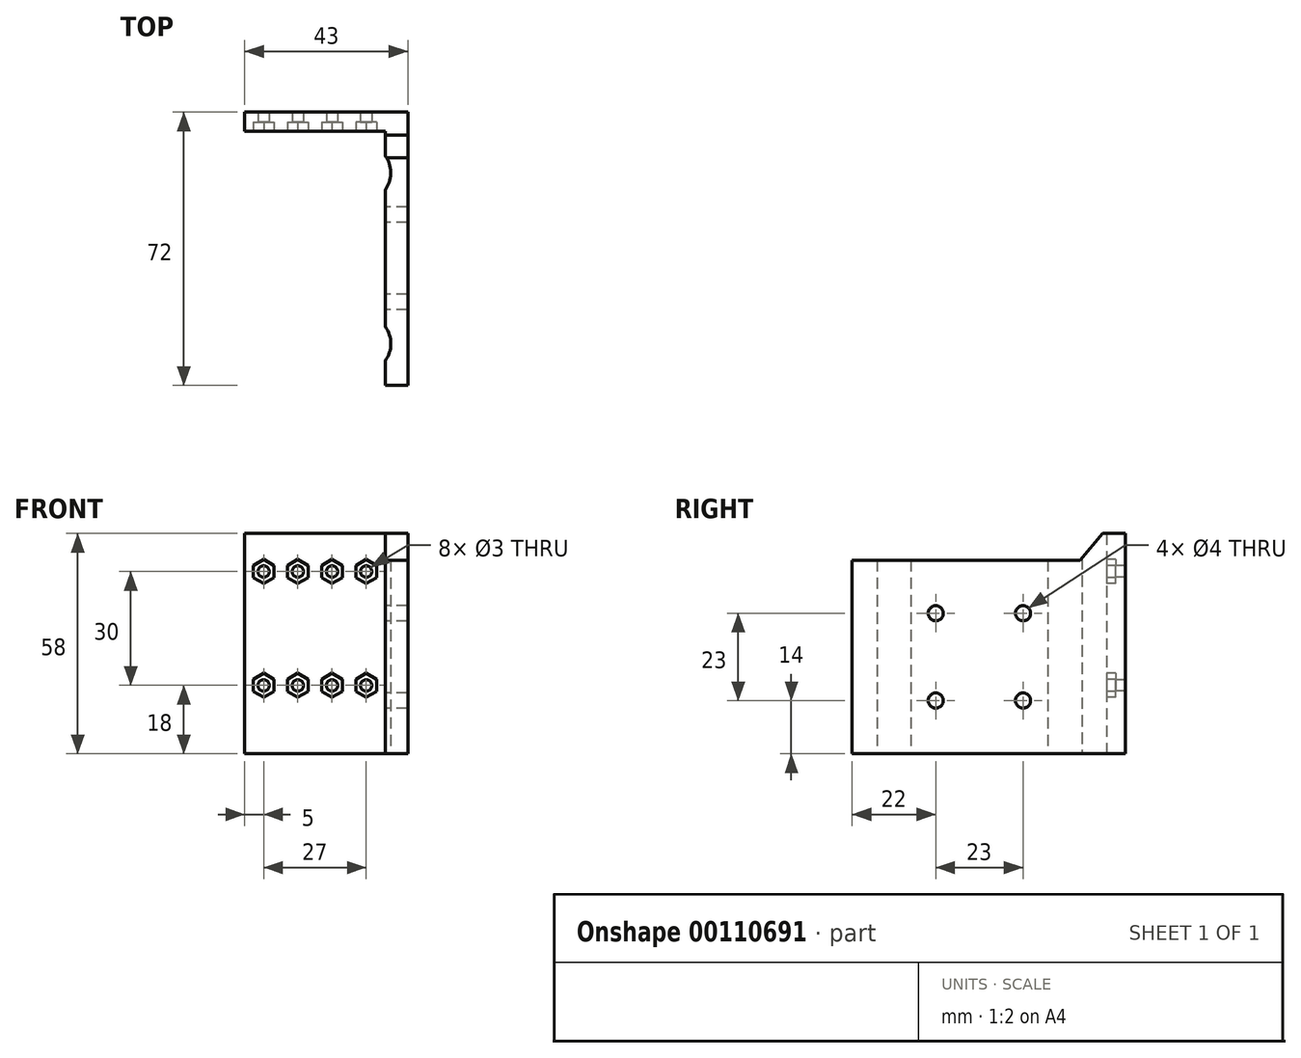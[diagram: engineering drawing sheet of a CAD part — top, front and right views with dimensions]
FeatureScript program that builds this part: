
annotation { "Feature Type Name" : "Feature", "Feature Type Description" : "" }
export const myFeature = defineFeature(function(context is Context, id is Id, definition is map)
    precondition{}
    {
        {
            var Q0;
            Q0=qCreatedBy(makeId("Top.planeOp"),FACE);
            var sketch = newSketch(context, id + "F0", { "sketchPlane" : qUnion([Q0])});
            skLineSegment(sketch, "E0", {"start": v(0, 0) * mm, "end": v(0, 67) * mm});
            skLineSegment(sketch, "E1", {"start": v(0, 67) * mm, "end": v(-37, 67) * mm});
            skLineSegment(sketch, "E2", {"start": v(-37, 67) * mm, "end": v(-37, 72) * mm});
            skLineSegment(sketch, "E3", {"start": v(-37, 72) * mm, "end": v(6, 72) * mm});
            skLineSegment(sketch, "E4", {"start": v(6, 72) * mm, "end": v(6, 0) * mm});
            skLineSegment(sketch, "E5", {"start": v(6, 0) * mm, "end": v(0, 0) * mm});
            skSolve(sketch);
        }
        {
            var Q0;
            Q0 = qSketchRegion(id + "F0", true);
            extrude(context, id + "F1", {"entities" : qUnion([Q0]), "depth" : 58 * mm});
        }
        {
            var Q0;
            Q0=makeQuery(id+"F1.opExtrude","SWEPT_FACE",FACE,{"disambiguationData":[OSD([sQuery(id+"F0.wireOp",EDGE,"E0")])]});
            var sketch = newSketch(context, id + "F2", { "sketchPlane" : qUnion([Q0])});
            skLineSegment(sketch, "E6", {"start": v(-33.5, 0) * mm, "end": v(-33.5, 58) * mm, "construction": true});
            skCircle(sketch, "E7", {"center": v(-45, 14) * mm, "radius": 2 * mm});
            skCircle(sketch, "E8", {"center": v(-45, 37) * mm, "radius": 2 * mm});
            skCircle(sketch, "E9", {"center": v(-22, 14) * mm, "radius": 2 * mm});
            skCircle(sketch, "E10", {"center": v(-22, 37) * mm, "radius": 2 * mm});
            skLineSegment(sketch, "E11", {"start": v(0, 25.5) * mm, "end": v(-67, 25.5) * mm, "construction": true});
            skSolve(sketch);
        }
        {
            var Q0;
            Q0=makeQuery(id+"F2.imprint","IMPRINT",FACE,{"disambiguationData":[TD([[makeQuery(id+"F2.imprint","IMPRINT",EDGE,{"derivedFrom":sQuery(id+"F2.wireOp",EDGE,"E8")}),1.0]])]});
            var Q1;
            Q1=makeQuery(id+"F2.imprint","IMPRINT",FACE,{"disambiguationData":[TD([[makeQuery(id+"F2.imprint","IMPRINT",EDGE,{"derivedFrom":sQuery(id+"F2.wireOp",EDGE,"E7")}),1.0]])]});
            var Q2;
            Q2=makeQuery(id+"F2.imprint","IMPRINT",FACE,{"disambiguationData":[TD([[makeQuery(id+"F2.imprint","IMPRINT",EDGE,{"derivedFrom":sQuery(id+"F2.wireOp",EDGE,"E9")}),1.0]])]});
            var Q3;
            Q3=makeQuery(id+"F2.imprint","IMPRINT",FACE,{"disambiguationData":[TD([[makeQuery(id+"F2.imprint","IMPRINT",EDGE,{"derivedFrom":sQuery(id+"F2.wireOp",EDGE,"E10")}),1.0]])]});
            extrude(context, id + "F3", {"entities" : qUnion([Q0, Q1, Q2, Q3]), "operationType" : NewBodyOperationType.REMOVE, "endBound" : BoundingType.THROUGH_ALL, "oppositeDirection" : true, "depth" : 25 * mm});
        }
        {
            var Q0;
            Q0=makeQuery(id+"F0.imprint","IMPRINT",FACE,{"disambiguationData":[TD([[makeQuery(id+"F0.imprint","IMPRINT",EDGE,{"derivedFrom":sQuery(id+"F0.wireOp",EDGE,"E0")}),-1.0]])]});
            var sketch = newSketch(context, id + "F4", { "sketchPlane" : qUnion([Q0])});
            skLineSegment(sketch, "E12", {"start": v(0, 33.5) * mm, "end": v(25.28, 33.5) * mm, "construction": true});
            skCircle(sketch, "E13", {"center": v(-6, 11) * mm, "radius": 7.5 * mm});
            skCircle(sketch, "E14.MirrorC", {"center": v(-6, 56) * mm, "radius": 7.5 * mm});
            skSolve(sketch);
        }
        {
            var Q0;
            Q0 = qSketchRegion(id + "F4", true);
            extrude(context, id + "F5", {"entities" : qUnion([Q0]), "operationType" : NewBodyOperationType.REMOVE, "endBound" : BoundingType.THROUGH_ALL, "depth" : 25 * mm});
        }
        {
            var Q0;
            Q0=makeQuery(id+"F1.opExtrude","SWEPT_FACE",FACE,{"disambiguationData":[OSD([sQuery(id+"F0.wireOp",EDGE,"E4")])]});
            var sketch = newSketch(context, id + "F6", { "sketchPlane" : qUnion([Q0])});
            skLineSegment(sketch, "E15", {"start": v(66, 58) * mm, "end": v(60, 51) * mm});
            skLineSegment(sketch, "E16", {"start": v(60, 51) * mm, "end": v(0, 51) * mm});
            skLineSegment(sketch, "E17", {"start": v(0, 51) * mm, "end": v(0, 58) * mm});
            skLineSegment(sketch, "E18", {"start": v(0, 58) * mm, "end": v(66, 58) * mm});
            skSolve(sketch);
        }
        {
            var Q0;
            Q0 = qSketchRegion(id + "F6", true);
            extrude(context, id + "F7", {"entities" : qUnion([Q0]), "operationType" : NewBodyOperationType.REMOVE, "endBound" : BoundingType.THROUGH_ALL, "oppositeDirection" : true, "depth" : 25 * mm});
        }
        {
            var Q0;
            Q0=makeQuery(id+"F1.opExtrude","SWEPT_FACE",FACE,{"disambiguationData":[OSD([sQuery(id+"F0.wireOp",EDGE,"E1")])]});
            var sketch = newSketch(context, id + "F8", { "sketchPlane" : qUnion([Q0])});
            skLineSegment(sketch, "E19", {"start": v(0, 33) * mm, "end": v(-37, 33) * mm, "construction": true});
            skCircle(sketch, "E20", {"center": v(-5, 48) * mm, "radius": 1.5 * mm});
            skCircle(sketch, "E21.cCircle", {"center": v(-5, 48) * mm, "radius": 2.75 * mm, "construction": true});
            skLineSegment(sketch, "E21.0", {"start": v(-7.75, 46.41) * mm, "end": v(-7.75, 49.59) * mm});
            skLineSegment(sketch, "E21.1", {"start": v(-7.75, 49.59) * mm, "end": v(-5, 51.18) * mm});
            skLineSegment(sketch, "E21.2", {"start": v(-5, 51.18) * mm, "end": v(-2.25, 49.59) * mm});
            skLineSegment(sketch, "E21.3", {"start": v(-2.25, 49.59) * mm, "end": v(-2.25, 46.41) * mm});
            skLineSegment(sketch, "E21.4", {"start": v(-2.25, 46.41) * mm, "end": v(-5, 44.82) * mm});
            skLineSegment(sketch, "E21.5", {"start": v(-5, 44.82) * mm, "end": v(-7.75, 46.41) * mm});
            skPoint(sketch, "E21.0.midPoint", {"position": v(-7.75, 48) * mm});
            skCircle(sketch, "E22.0.1.0", {"center": v(-5, 18) * mm, "radius": 1.5 * mm});
            skCircle(sketch, "E22.0.1.1", {"center": v(-5, 18) * mm, "radius": 2.75 * mm, "construction": true});
            skPoint(sketch, "E22.0.1.2", {"position": v(-7.75, 18) * mm});
            skLineSegment(sketch, "E22.0.1.3", {"start": v(-2.25, 19.59) * mm, "end": v(-2.25, 16.41) * mm});
            skLineSegment(sketch, "E22.0.1.4", {"start": v(-2.25, 16.41) * mm, "end": v(-5, 14.82) * mm});
            skLineSegment(sketch, "E22.0.1.5", {"start": v(-5, 14.82) * mm, "end": v(-7.75, 16.41) * mm});
            skLineSegment(sketch, "E22.0.1.6", {"start": v(-7.75, 16.41) * mm, "end": v(-7.75, 19.59) * mm});
            skLineSegment(sketch, "E22.0.1.7", {"start": v(-7.75, 19.59) * mm, "end": v(-5, 21.18) * mm});
            skLineSegment(sketch, "E22.0.1.8", {"start": v(-5, 21.18) * mm, "end": v(-2.25, 19.59) * mm});
            skCircle(sketch, "E22.1.0.0", {"center": v(-14, 48) * mm, "radius": 1.5 * mm});
            skCircle(sketch, "E22.1.0.1", {"center": v(-14, 48) * mm, "radius": 2.75 * mm, "construction": true});
            skPoint(sketch, "E22.1.0.2", {"position": v(-16.75, 48) * mm});
            skLineSegment(sketch, "E22.1.0.3", {"start": v(-11.25, 49.59) * mm, "end": v(-11.25, 46.41) * mm});
            skLineSegment(sketch, "E22.1.0.4", {"start": v(-11.25, 46.41) * mm, "end": v(-14, 44.82) * mm});
            skLineSegment(sketch, "E22.1.0.5", {"start": v(-14, 44.82) * mm, "end": v(-16.75, 46.41) * mm});
            skLineSegment(sketch, "E22.1.0.6", {"start": v(-16.75, 46.41) * mm, "end": v(-16.75, 49.59) * mm});
            skLineSegment(sketch, "E22.1.0.7", {"start": v(-16.75, 49.59) * mm, "end": v(-14, 51.18) * mm});
            skLineSegment(sketch, "E22.1.0.8", {"start": v(-14, 51.18) * mm, "end": v(-11.25, 49.59) * mm});
            skCircle(sketch, "E22.1.1.0", {"center": v(-14, 18) * mm, "radius": 1.5 * mm});
            skCircle(sketch, "E22.1.1.1", {"center": v(-14, 18) * mm, "radius": 2.75 * mm, "construction": true});
            skPoint(sketch, "E22.1.1.2", {"position": v(-16.75, 18) * mm});
            skLineSegment(sketch, "E22.1.1.3", {"start": v(-11.25, 19.59) * mm, "end": v(-11.25, 16.41) * mm});
            skLineSegment(sketch, "E22.1.1.4", {"start": v(-11.25, 16.41) * mm, "end": v(-14, 14.82) * mm});
            skLineSegment(sketch, "E22.1.1.5", {"start": v(-14, 14.82) * mm, "end": v(-16.75, 16.41) * mm});
            skLineSegment(sketch, "E22.1.1.6", {"start": v(-16.75, 16.41) * mm, "end": v(-16.75, 19.59) * mm});
            skLineSegment(sketch, "E22.1.1.7", {"start": v(-16.75, 19.59) * mm, "end": v(-14, 21.18) * mm});
            skLineSegment(sketch, "E22.1.1.8", {"start": v(-14, 21.18) * mm, "end": v(-11.25, 19.59) * mm});
            skCircle(sketch, "E22.2.0.0", {"center": v(-23, 48) * mm, "radius": 1.5 * mm});
            skCircle(sketch, "E22.2.0.1", {"center": v(-23, 48) * mm, "radius": 2.75 * mm, "construction": true});
            skPoint(sketch, "E22.2.0.2", {"position": v(-25.75, 48) * mm});
            skLineSegment(sketch, "E22.2.0.3", {"start": v(-20.25, 49.59) * mm, "end": v(-20.25, 46.41) * mm});
            skLineSegment(sketch, "E22.2.0.4", {"start": v(-20.25, 46.41) * mm, "end": v(-23, 44.82) * mm});
            skLineSegment(sketch, "E22.2.0.5", {"start": v(-23, 44.82) * mm, "end": v(-25.75, 46.41) * mm});
            skLineSegment(sketch, "E22.2.0.6", {"start": v(-25.75, 46.41) * mm, "end": v(-25.75, 49.59) * mm});
            skLineSegment(sketch, "E22.2.0.7", {"start": v(-25.75, 49.59) * mm, "end": v(-23, 51.18) * mm});
            skLineSegment(sketch, "E22.2.0.8", {"start": v(-23, 51.18) * mm, "end": v(-20.25, 49.59) * mm});
            skCircle(sketch, "E22.2.1.0", {"center": v(-23, 18) * mm, "radius": 1.5 * mm});
            skCircle(sketch, "E22.2.1.1", {"center": v(-23, 18) * mm, "radius": 2.75 * mm, "construction": true});
            skPoint(sketch, "E22.2.1.2", {"position": v(-25.75, 18) * mm});
            skLineSegment(sketch, "E22.2.1.3", {"start": v(-20.25, 19.59) * mm, "end": v(-20.25, 16.41) * mm});
            skLineSegment(sketch, "E22.2.1.4", {"start": v(-20.25, 16.41) * mm, "end": v(-23, 14.82) * mm});
            skLineSegment(sketch, "E22.2.1.5", {"start": v(-23, 14.82) * mm, "end": v(-25.75, 16.41) * mm});
            skLineSegment(sketch, "E22.2.1.6", {"start": v(-25.75, 16.41) * mm, "end": v(-25.75, 19.59) * mm});
            skLineSegment(sketch, "E22.2.1.7", {"start": v(-25.75, 19.59) * mm, "end": v(-23, 21.18) * mm});
            skLineSegment(sketch, "E22.2.1.8", {"start": v(-23, 21.18) * mm, "end": v(-20.25, 19.59) * mm});
            skCircle(sketch, "E22.3.0.0", {"center": v(-32, 48) * mm, "radius": 1.5 * mm});
            skCircle(sketch, "E22.3.0.1", {"center": v(-32, 48) * mm, "radius": 2.75 * mm, "construction": true});
            skPoint(sketch, "E22.3.0.2", {"position": v(-34.75, 48) * mm});
            skLineSegment(sketch, "E22.3.0.3", {"start": v(-29.25, 49.59) * mm, "end": v(-29.25, 46.41) * mm});
            skLineSegment(sketch, "E22.3.0.4", {"start": v(-29.25, 46.41) * mm, "end": v(-32, 44.82) * mm});
            skLineSegment(sketch, "E22.3.0.5", {"start": v(-32, 44.82) * mm, "end": v(-34.75, 46.41) * mm});
            skLineSegment(sketch, "E22.3.0.6", {"start": v(-34.75, 46.41) * mm, "end": v(-34.75, 49.59) * mm});
            skLineSegment(sketch, "E22.3.0.7", {"start": v(-34.75, 49.59) * mm, "end": v(-32, 51.18) * mm});
            skLineSegment(sketch, "E22.3.0.8", {"start": v(-32, 51.18) * mm, "end": v(-29.25, 49.59) * mm});
            skCircle(sketch, "E22.3.1.0", {"center": v(-32, 18) * mm, "radius": 1.5 * mm});
            skCircle(sketch, "E22.3.1.1", {"center": v(-32, 18) * mm, "radius": 2.75 * mm, "construction": true});
            skPoint(sketch, "E22.3.1.2", {"position": v(-34.75, 18) * mm});
            skLineSegment(sketch, "E22.3.1.3", {"start": v(-29.25, 19.59) * mm, "end": v(-29.25, 16.41) * mm});
            skLineSegment(sketch, "E22.3.1.4", {"start": v(-29.25, 16.41) * mm, "end": v(-32, 14.82) * mm});
            skLineSegment(sketch, "E22.3.1.5", {"start": v(-32, 14.82) * mm, "end": v(-34.75, 16.41) * mm});
            skLineSegment(sketch, "E22.3.1.6", {"start": v(-34.75, 16.41) * mm, "end": v(-34.75, 19.59) * mm});
            skLineSegment(sketch, "E22.3.1.7", {"start": v(-34.75, 19.59) * mm, "end": v(-32, 21.18) * mm});
            skLineSegment(sketch, "E22.3.1.8", {"start": v(-32, 21.18) * mm, "end": v(-29.25, 19.59) * mm});
            skLineSegment(sketch, "E22.direction1", {"start": v(-7.75, 46.41) * mm, "end": v(-16.75, 46.41) * mm, "construction": true});
            skLineSegment(sketch, "E22.direction2", {"start": v(-7.75, 46.41) * mm, "end": v(-7.75, 16.41) * mm, "construction": true});
            skSolve(sketch);
        }
        {
            var Q0;
            Q0 = qSketchRegion(id + "F8", true);
            extrude(context, id + "F9", {"entities" : qUnion([Q0]), "operationType" : NewBodyOperationType.REMOVE, "oppositeDirection" : true, "depth" : 2.4 * mm});
        }
        {
            var Q0;
            Q0=makeQuery(id+"F8.imprint","IMPRINT",FACE,{"disambiguationData":[TD([[makeQuery(id+"F8.imprint","IMPRINT",EDGE,{"derivedFrom":sQuery(id+"F8.wireOp",EDGE,"E22.3.0.0")}),1.0]])]});
            var Q1;
            Q1=makeQuery(id+"F8.imprint","IMPRINT",FACE,{"disambiguationData":[TD([[makeQuery(id+"F8.imprint","IMPRINT",EDGE,{"derivedFrom":sQuery(id+"F8.wireOp",EDGE,"E22.2.0.0")}),1.0]])]});
            var Q2;
            Q2=makeQuery(id+"F8.imprint","IMPRINT",FACE,{"disambiguationData":[TD([[makeQuery(id+"F8.imprint","IMPRINT",EDGE,{"derivedFrom":sQuery(id+"F8.wireOp",EDGE,"E22.1.0.0")}),1.0]])]});
            var Q3;
            Q3=makeQuery(id+"F8.imprint","IMPRINT",FACE,{"disambiguationData":[TD([[makeQuery(id+"F8.imprint","IMPRINT",EDGE,{"derivedFrom":sQuery(id+"F8.wireOp",EDGE,"E20")}),1.0]])]});
            var Q4;
            Q4=makeQuery(id+"F8.imprint","IMPRINT",FACE,{"disambiguationData":[TD([[makeQuery(id+"F8.imprint","IMPRINT",EDGE,{"derivedFrom":sQuery(id+"F8.wireOp",EDGE,"E22.3.1.0")}),1.0]])]});
            var Q5;
            Q5=makeQuery(id+"F8.imprint","IMPRINT",FACE,{"disambiguationData":[TD([[makeQuery(id+"F8.imprint","IMPRINT",EDGE,{"derivedFrom":sQuery(id+"F8.wireOp",EDGE,"E22.2.1.0")}),1.0]])]});
            var Q6;
            Q6=makeQuery(id+"F8.imprint","IMPRINT",FACE,{"disambiguationData":[TD([[makeQuery(id+"F8.imprint","IMPRINT",EDGE,{"derivedFrom":sQuery(id+"F8.wireOp",EDGE,"E22.1.1.0")}),1.0]])]});
            var Q7;
            Q7=makeQuery(id+"F8.imprint","IMPRINT",FACE,{"disambiguationData":[TD([[makeQuery(id+"F8.imprint","IMPRINT",EDGE,{"derivedFrom":sQuery(id+"F8.wireOp",EDGE,"E22.0.1.0")}),1.0]])]});
            extrude(context, id + "F10", {"entities" : qUnion([Q0, Q1, Q2, Q3, Q4, Q5, Q6, Q7]), "operationType" : NewBodyOperationType.REMOVE, "endBound" : BoundingType.THROUGH_ALL, "oppositeDirection" : true, "depth" : 25 * mm});
        }
    });
